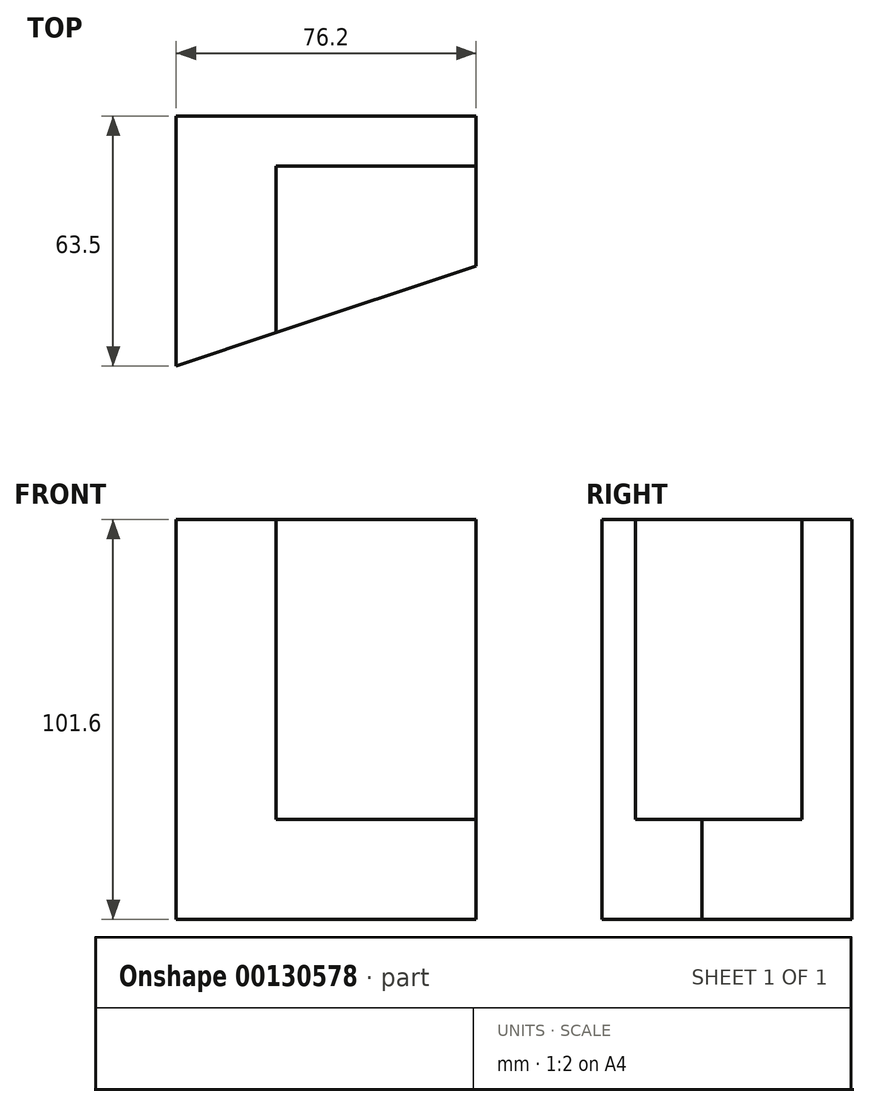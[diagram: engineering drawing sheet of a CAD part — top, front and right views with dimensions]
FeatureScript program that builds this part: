
annotation { "Feature Type Name" : "Feature", "Feature Type Description" : "" }
export const myFeature = defineFeature(function(context is Context, id is Id, definition is map)
    precondition{}
    {
        {
            var Q0;
            Q0=qCreatedBy(makeId("Top.planeOp"),FACE);
            var sketch = newSketch(context, id + "F0", { "sketchPlane" : qUnion([Q0])});
            skLineSegment(sketch, "E0", {"start": v(0, 0) * mm, "end": v(0, 63.5) * mm});
            skLineSegment(sketch, "E1", {"start": v(0, 63.5) * mm, "end": v(76.2, 63.5) * mm});
            skLineSegment(sketch, "E2", {"start": v(76.2, 63.5) * mm, "end": v(76.2, 25.4) * mm});
            skLineSegment(sketch, "E3", {"start": v(76.2, 25.4) * mm, "end": v(0, 0) * mm});
            skLineSegment(sketch, "E4", {"start": v(76.2, 50.8) * mm, "end": v(25.4, 50.8) * mm});
            skLineSegment(sketch, "E5", {"start": v(25.4, 50.8) * mm, "end": v(25.4, 8.47) * mm});
            skSolve(sketch);
        }
        {
            var Q0;
            {var subQ1=sQuery(id+"F0.wireOp",EDGE,"E0");Q0=makeQuery(id+"F0.imprint","IMPRINT",FACE,{"disambiguationData":[TD([[makeQuery(id+"F0.imprint","IMPRINT",EDGE,{"derivedFrom":subQ1}),-1.0]])]});}
            extrude(context, id + "F1", {"entities" : qUnion([Q0]), "depth" : 101.6 * mm});
        }
        {
            var Q0;
            {var subQ3=sQuery(id+"F0.wireOp",EDGE,"E4");Q0=makeQuery(id+"F0.imprint","IMPRINT",FACE,{"disambiguationData":[TD([[makeQuery(id+"F0.imprint","IMPRINT",EDGE,{"derivedFrom":subQ3}),1.0]])]});}
            extrude(context, id + "F2", {"entities" : qUnion([Q0]), "operationType" : NewBodyOperationType.ADD, "depth" : 25.4 * mm});
        }
    });
